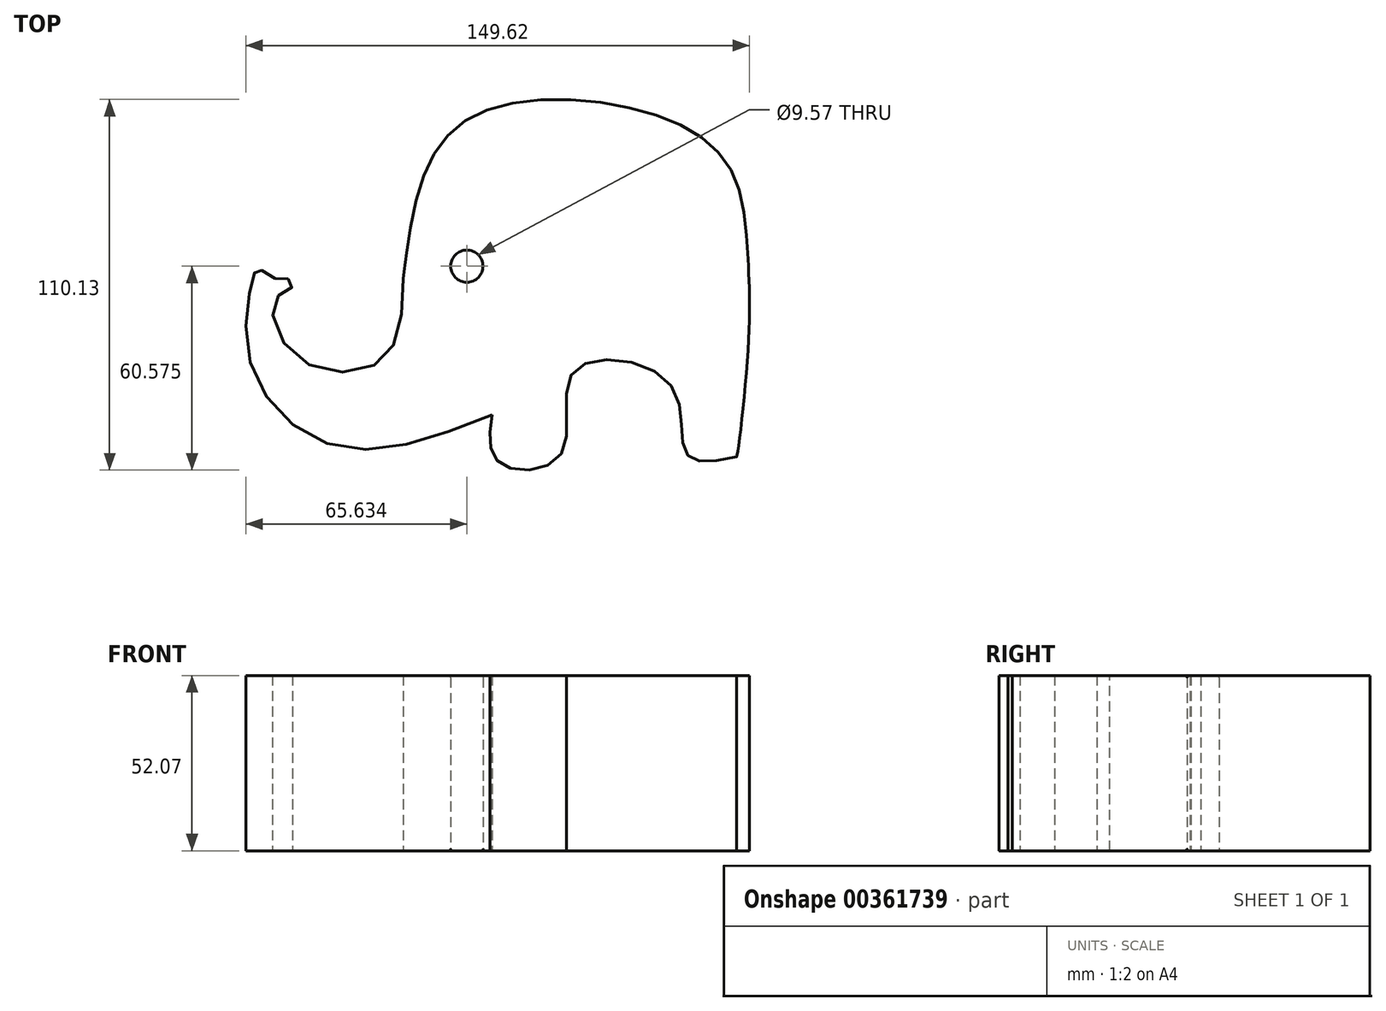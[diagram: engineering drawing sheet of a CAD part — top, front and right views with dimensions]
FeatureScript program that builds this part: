
annotation { "Feature Type Name" : "Feature", "Feature Type Description" : "" }
export const myFeature = defineFeature(function(context is Context, id is Id, definition is map)
    precondition{}
    {
        {
            var Q0;
            Q0=qCreatedBy(makeId("Top.planeOp"),FACE);
            var sketch = newSketch(context, id + "F0", { "sketchPlane" : qUnion([Q0])});
            skFitSpline(sketch, "E0", {"points": [v(55.53, 17.62) * mm, v(49.1, 46.44) * mm, v(18.88, 62.94) * mm, v(-26.16, 60.15) * mm, v(-43.5, 33.57) * mm, v(-46.86, 11.75) * mm, v(-46.86, 12.3) * mm], "startDerivative": vector(-9.38, 168.84) * mm, "endDerivative": vector(0.82, 33.29) * mm});
            skFitSpline(sketch, "E1", {"points": [v(55.53, -40.28) * mm, v(37.35, -40.28) * mm, v(32.31, -19.3) * mm, v(3.78, -15.67) * mm, v(0, -40.28) * mm, v(-18.04, -43.08) * mm, v(-20.56, -28.54) * mm], "startDerivative": vector(-149.34, -35.23) * mm, "endDerivative": vector(15.45, 125.22) * mm});
            skFitSpline(sketch, "E2", {"points": [v(-46.86, 11.75) * mm, v(-53.57, -12.59) * mm, v(-78.47, -11.47) * mm, v(-84.9, 5.87) * mm, v(-79.87, 9.51) * mm, v(-80.99, 11.75) * mm, v(-85.47, 12.02) * mm, v(-89.94, 14.83) * mm, v(-91.62, 12.02) * mm, v(-92.18, -13.7) * mm, v(-66.16, -38.05) * mm, v(-20.56, -28.54) * mm], "startDerivative": vector(-7.96, -248.23) * mm, "endDerivative": vector(296.82, 118.43) * mm});
            skFitSpline(sketch, "E3", {"points": [v(55.53, 17.62) * mm, v(55.53, -9.54) * mm, v(52.16, -41.07) * mm, v(52.11, -41.08) * mm], "startDerivative": vector(2.4, -48.3) * mm, "endDerivative": vector(-2.17, 0.9) * mm});
            skCircle(sketch, "E4", {"center": v(-28.02, 15.58) * mm, "radius": 4.78 * mm});
            skSolve(sketch);
        }
        {
            var Q0;
            Q0 = qSketchRegion(id + "F0", true);
            extrude(context, id + "F1", {"entities" : qUnion([Q0]), "depth" : 52.07 * mm});
        }
        {
            var Q0;
            Q0=makeQuery(id+"F1.opExtrude","CAP_EDGE",EDGE,{"disambiguationData":[OSD([sQuery(id+"F0.wireOp",EDGE,"E4")])],"isStart":false});
            fillet(context, id + "F2", {"entities" : qUnion([Q0]), "radius" : 0.64 * mm, "tangentPropagation" : true, "allowEdgeOverflow" : false});
        }
        {
            var Q0;
            Q0=makeQuery(id+"F1.opExtrude","CAP_EDGE",EDGE,{"disambiguationData":[OSD([sQuery(id+"F0.wireOp",EDGE,"E4")])],"isStart":true});
            fillet(context, id + "F3", {"entities" : qUnion([Q0]), "radius" : 0.64 * mm, "tangentPropagation" : true, "allowEdgeOverflow" : false});
        }
    });
